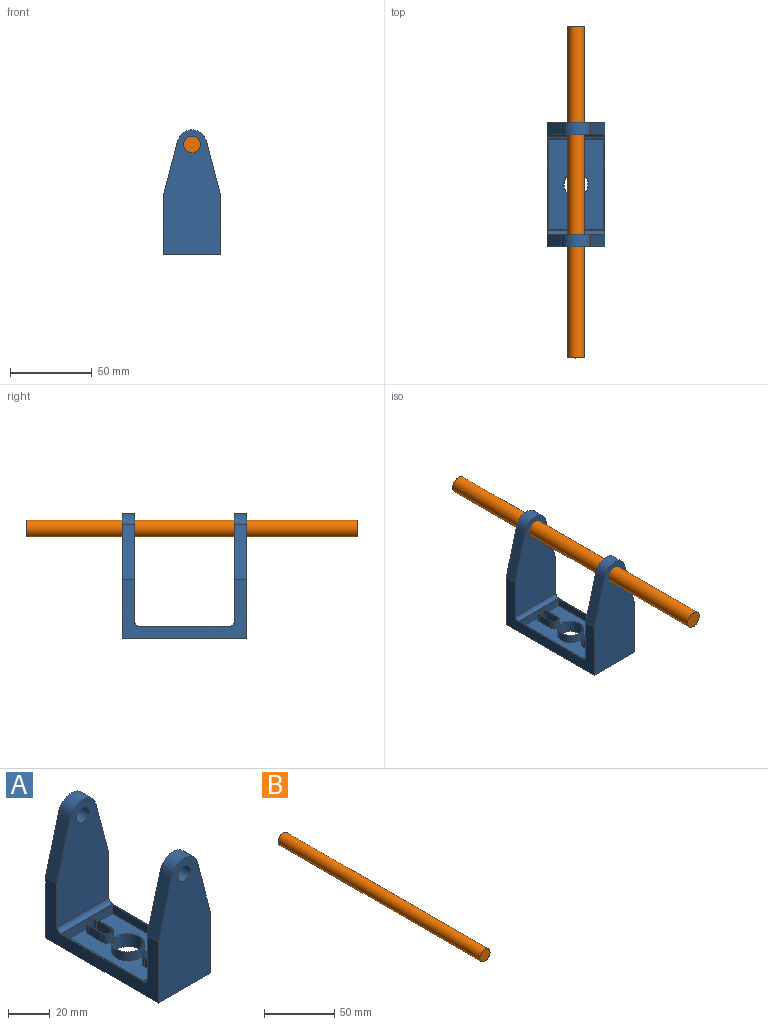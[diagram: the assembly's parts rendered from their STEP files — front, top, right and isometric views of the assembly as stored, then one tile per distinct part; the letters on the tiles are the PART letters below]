
ASSEMBLY  parts=2 mates=1
PART A: 44 faces, bbox 35.2x76.2x76 mm
  f0: plane 15.59x15.59mm, normal (0,0,1), area 24.1mm2, adj f19,f39
  f1: plane 15.9x6.52mm, normal (0,0,1), area 19.1mm2, adj f20,f21,f22,f23,f33,f34,f35,f40
  f2: plane 15.9x6.52mm, normal (0,0,1), area 19.1mm2, adj f24,f25,f26,f27,f36,f37,f38,f41
  f3: plane 76.2x35.15mm, normal (0,0,-1), area 2360.7mm2, adj f6,f7,f15,f16,f19,f20,f21,f22
  f4: plane 55.88x35.15mm, normal (0,0,1), area 91.5mm2, adj f6,f7,f28,f29,f30,f31,f32,f42
  f5: plane 33.68x8.87mm, normal (-0.97,0,0.25), area 265.4mm2, adj f6,f10,f15,f17
  f6: plane 76.2x35.64mm, normal (-1,0,0), area 991.6mm2, adj f3,f4,f5,f11,f15,f16,f17,f18
  f7: plane 76.2x35.64mm, normal (1,0,0), area 991.6mm2, adj f3,f4,f8,f12,f15,f16,f17,f18
  f8: plane 33.68x8.87mm, normal (0.97,0,0.25), area 265.4mm2, adj f7,f10,f15,f17
  f9: cylinder r=4.25mm len=8.5mm, axis (0,1,0), area 203.6mm2, adj f15,f17
  f10: cylinder r=9mm len=17.42mm, axis (0,1,0), area 180.2mm2, adj f5,f8,f15,f17
  f11: plane 33.68x8.87mm, normal (-0.97,0,0.25), area 265.4mm2, adj f6,f14,f16,f18
  f12: plane 33.68x8.87mm, normal (0.97,0,0.25), area 265.4mm2, adj f7,f14,f16,f18
  f13: cylinder r=4.25mm len=8.5mm, axis (0,1,0), area 203.6mm2, adj f16,f18
  f14: cylinder r=9mm len=17.42mm, axis (0,1,0), area 180.2mm2, adj f11,f12,f16,f18
  f15: plane 76.03x35.15mm, normal (0,-1,0), area 2167.7mm2, adj f3,f5,f6,f7,f8,f9,f10
  f16: plane 76.03x35.15mm, normal (0,1,0), area 2167.7mm2, adj f3,f6,f7,f11,f12,f13,f14
  f17: plane 66.18x35.15mm, normal (0,1,0), area 1821.4mm2, adj f5,f6,f7,f8,f9,f10,f28
  f18: plane 66.18x35.15mm, normal (0,-1,0), area 1821.4mm2, adj f6,f7,f11,f12,f13,f14,f29
  f19: cylinder r=7.29mm len=14.57mm, axis (0,0,1), area 334.7mm2, adj f0,f3
  f20: cylinder r=2.75mm len=7.31mm, axis (0,0,1), area 63.3mm2, adj f1,f3,f21,f23
  f21: plane 9.38x7.31mm, normal (1,0,0), area 68.6mm2, adj f1,f3,f20,f22
  f22: cylinder r=2.75mm len=7.31mm, axis (0,0,1), area 63.3mm2, adj f1,f3,f21,f23
  f23: plane 9.38x7.31mm, normal (-1,0,0), area 68.6mm2, adj f1,f3,f20,f22
  f24: plane 9.38x7.31mm, normal (1,0,0), area 68.6mm2, adj f2,f3,f25,f27
  f25: cylinder r=2.75mm len=7.31mm, axis (0,0,1), area 63.3mm2, adj f2,f3,f24,f26
  f26: plane 9.38x7.31mm, normal (-1,0,0), area 68.6mm2, adj f2,f3,f25,f27
  f27: cylinder r=2.75mm len=7.31mm, axis (0,0,1), area 63.3mm2, adj f2,f3,f24,f26
  f28: cylinder r=2.54mm len=35.15mm, axis (1,0,0), area 140.2mm2, adj f4,f6,f7,f17
  f29: cylinder r=2.54mm len=35.15mm, axis (-1,0,0), area 140.2mm2, adj f4,f6,f7,f18
  f30: plane 54.86x5.08mm, normal (1,0,0), area 278.7mm2, adj f4,f31,f42,f43
  f31: plane 34.13x5.08mm, normal (0,1,0), area 173.4mm2, adj f4,f30,f32,f43
  f32: plane 54.86x5.08mm, normal (-1,0,0), area 278.7mm2, adj f4,f31,f42,f43
  f33: cylinder r=3.26mm len=6.52mm, axis (0,0,1), area 52.1mm2, adj f1,f34,f40,f43
  f34: plane 9.38x5.08mm, normal (-1,0,0), area 47.6mm2, adj f1,f33,f35,f43
  f35: cylinder r=3.26mm len=6.52mm, axis (0,0,1), area 52.1mm2, adj f1,f34,f40,f43
  f36: plane 9.38x5.08mm, normal (-1,0,0), area 47.6mm2, adj f2,f37,f41,f43
  f37: cylinder r=3.26mm len=6.52mm, axis (0,0,1), area 52.1mm2, adj f2,f36,f38,f43
  f38: plane 9.38x5.08mm, normal (1,0,0), area 47.6mm2, adj f2,f37,f41,f43
  f39: cylinder r=7.79mm len=15.59mm, axis (0,0,1), area 248.8mm2, adj f0,f43
  f40: plane 9.38x5.08mm, normal (1,0,0), area 47.6mm2, adj f1,f33,f35,f43
  f41: cylinder r=3.26mm len=6.52mm, axis (0,0,1), area 52.1mm2, adj f2,f36,f38,f43
  f42: plane 34.13x5.08mm, normal (0,-1,0), area 173.4mm2, adj f4,f30,f32,f43
  f43: plane 54.86x34.13mm, normal (0,0,1), area 1492.7mm2, adj f30,f31,f32,f33,f34,f35,f36,f37
PART B: 3 faces, bbox 10.3x203.2x10.3 mm
  f0: cylinder r=5.13mm len=203.2mm, axis (0,1,0), area 6550mm2, adj f1,f2
  f1: plane 10.26x10.26mm, normal (0,-1,0), area 82.7mm2, adj f0
  f2: plane 10.26x10.26mm, normal (0,1,0), area 82.7mm2, adj f0
PLACE A rot(axis=(0,-1,0),0deg) t=(-120.42,-18.44,-96.06)mm
PLACE B t=(-120.42,40.41,-64.68)mm
MATE cylindrical B.f0 <-> A.f9  axis (0,-1,0) through (-120.42,-162.79,-64.68)mm
